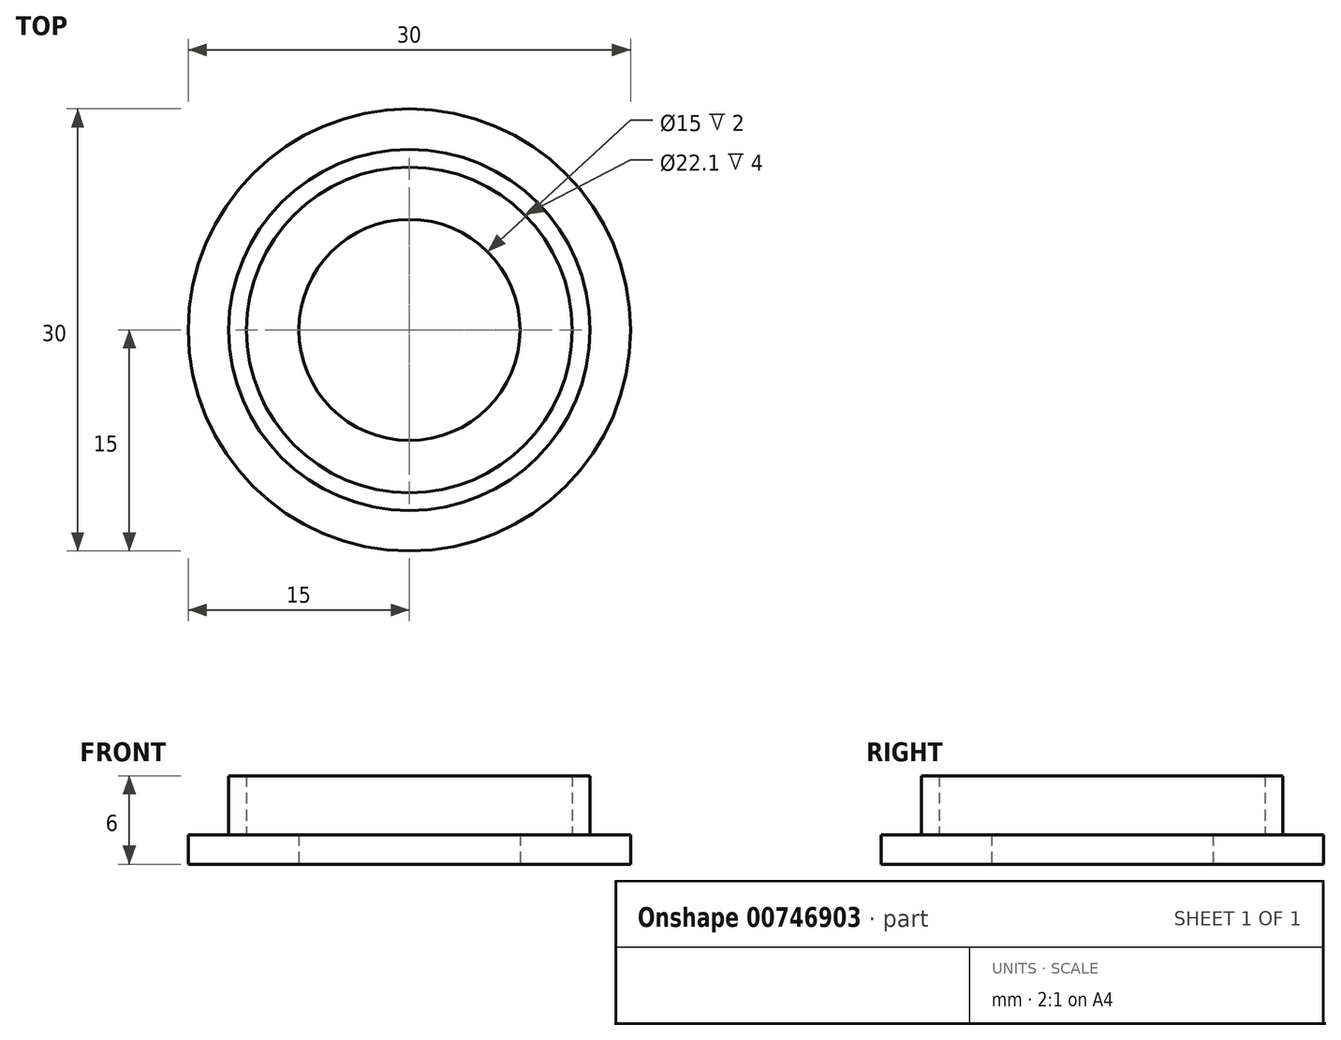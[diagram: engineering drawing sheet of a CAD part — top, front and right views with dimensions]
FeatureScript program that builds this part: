
annotation { "Feature Type Name" : "Feature", "Feature Type Description" : "" }
export const myFeature = defineFeature(function(context is Context, id is Id, definition is map)
    precondition{}
    {
        {
            var Q0;
            Q0=qCreatedBy(makeId("Top.planeOp"),FACE);
            var sketch = newSketch(context, id + "F0", { "sketchPlane" : qUnion([Q0])});
            skCircle(sketch, "E0", {"center": v(0, 0) * mm, "radius": 15 * mm});
            skCircle(sketch, "E1", {"center": v(0, 0) * mm, "radius": 7.5 * mm});
            skSolve(sketch);
        }
        {
            var Q0;
            Q0=makeQuery(id+"F0.imprint","IMPRINT",FACE,{"disambiguationData":[TD([[makeQuery(id+"F0.imprint","IMPRINT",EDGE,{"derivedFrom":sQuery(id+"F0.wireOp",EDGE,"E0")}),1.0]])]});
            extrude(context, id + "F1", {"entities" : qUnion([Q0]), "depth" : 2 * mm, "offsetDistance" : 25 * mm});
        }
        {
            var Q0;
            Q0=makeQuery(id+"F1.opExtrude","CAP_FACE",FACE,{"disambiguationData":[OSD([sQuery(id+"F0.wireOp",EDGE,"E0")])],"isStart":false});
            var sketch = newSketch(context, id + "F2", { "sketchPlane" : qUnion([Q0])});
            skCircle(sketch, "E2", {"center": v(0, 0) * mm, "radius": 11.05 * mm});
            skCircle(sketch, "E3", {"center": v(0, 0) * mm, "radius": 12.25 * mm});
            skSolve(sketch);
        }
        {
            var Q0;
            Q0=makeQuery(id+"F2.imprint","IMPRINT",FACE,{"disambiguationData":[TD([[makeQuery(id+"F2.imprint","IMPRINT",EDGE,{"derivedFrom":sQuery(id+"F2.wireOp",EDGE,"E2")}),-1.0]])]});
            extrude(context, id + "F3", {"entities" : qUnion([Q0]), "operationType" : NewBodyOperationType.ADD, "depth" : 4 * mm, "offsetDistance" : 25 * mm});
        }
    });
